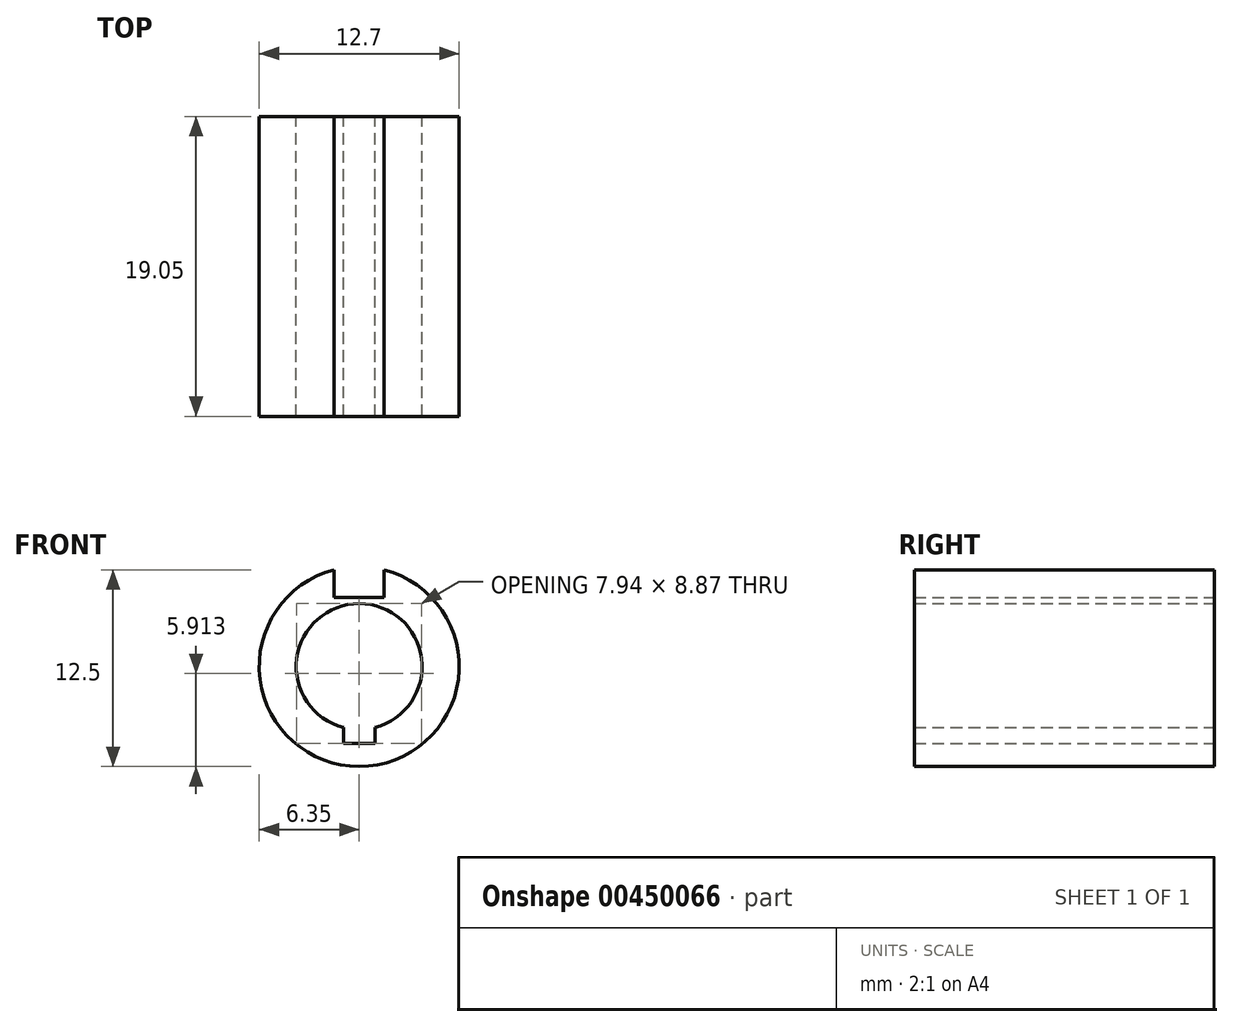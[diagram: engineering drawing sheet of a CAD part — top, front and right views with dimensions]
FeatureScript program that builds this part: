
annotation { "Feature Type Name" : "Feature", "Feature Type Description" : "" }
export const myFeature = defineFeature(function(context is Context, id is Id, definition is map)
    precondition{}
    {
        {
            var Q0;
            Q0=qCreatedBy(makeId("Front.planeOp"),FACE);
            var sketch = newSketch(context, id + "F0", { "sketchPlane" : qUnion([Q0])});
            skArc(sketch, "E0", {"start": v(-1.59, 6.15) * mm, "mid": v(0, -6.35) * mm, "end": v(1.59, 6.15) * mm});
            skArc(sketch, "E1", {"start": v(1, -3.87) * mm, "mid": v(0, 4) * mm, "end": v(-1, -3.87) * mm});
            skLineSegment(sketch, "E2", {"start": v(-1.59, 6.15) * mm, "end": v(-1.59, 4.4) * mm});
            skLineSegment(sketch, "E3", {"start": v(-1.59, 4.4) * mm, "end": v(1.59, 4.4) * mm});
            skLineSegment(sketch, "E4", {"start": v(1.59, 4.4) * mm, "end": v(1.59, 6.15) * mm});
            skLineSegment(sketch, "E5", {"start": v(-1, -3.87) * mm, "end": v(-1, -4.87) * mm});
            skLineSegment(sketch, "E6", {"start": v(-1, -4.87) * mm, "end": v(1, -4.87) * mm});
            skLineSegment(sketch, "E7", {"start": v(1, -4.87) * mm, "end": v(1, -3.87) * mm});
            skPoint(sketch, "E8", {"position": v(0, -4.87) * mm});
            skPoint(sketch, "E9", {"position": v(0, 4.4) * mm});
            skSolve(sketch);
        }
        {
            var Q0;
            {var subQ0=sQuery(id+"F0.wireOp",EDGE,"E2");Q0=makeQuery(id+"F0.imprint","IMPRINT",FACE,{"disambiguationData":[TD([[makeQuery(id+"F0.imprint","IMPRINT",EDGE,{"derivedFrom":subQ0}),-1.0]])]});}
            extrude(context, id + "F1", {"entities" : qUnion([Q0]), "depth" : 19.05 * mm});
        }
    });
